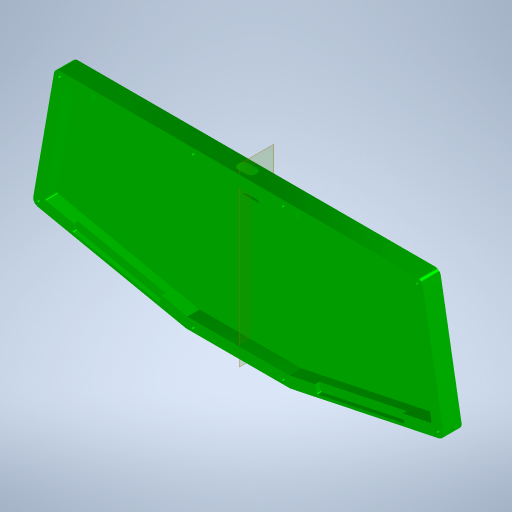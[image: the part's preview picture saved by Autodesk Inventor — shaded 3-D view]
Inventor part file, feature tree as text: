
AUTODESK INVENTOR PART (.ipt)
format: ipt  version: 2023 (Build 270158000, 158)  size: 662,016 bytes
history: native  units: mm
features: reference x28, extrude x7, sketch x7, other x6, fillet x5, plane x2, shell x1, mirror x1, hole x1, projected_geometry x1
ambient origin geometry x8: Origin, YZ Plane, XZ Plane, XY Plane, X Axis, Y Axis, Z Axis, Center Point
bodies: Body1 (feature_tree)
feature tree (59):
  extrude  "Extrusion1"  Depth=1.0mm
  shell  "Shell1"  Thickness=1.0mm
  extrude  "Extrusion7"  Depth=1.0mm
  plane  "Work Plane1"
  extrude  "Extrusion8"  Depth=17.0mm TaperAngle=0.0deg
  extrude  "Extrusion9"  Depth=8.0mm TaperAngle=0.0deg
  plane  "Work Plane2"
  extrude  "Extrusion10"  Depth=18.0mm
  mirror  "Mirror1"
  extrude  "Extrusion12"  Depth=2.0mm
  fillet  "Fillet1"  Radius=2.0mm
  fillet  "Fillet2"  Radius=2.0mm
  fillet  "Fillet3"  Radius=2.0mm
  extrude  "Extrusion13"  Depth=8.0mm TaperAngle=0.0deg
  fillet  "Fillet4"  Radius=98.02976mm
  fillet  "Fillet5"  Radius=10.0mm
  hole  "Hole1"  [1 undecoded]
  sketch  "Sketch1"  dims[d0=1.0mm d1=1.0mm d2=1.0mm]
  reference  "Reference1"
  reference  "Reference2"
  reference  "Reference3"
  reference  "Reference4"
  reference  "Reference5"
  sketch  "Sketch5"  dims[d3=1.0mm d4=1.0mm]
  projected_geometry  "Projected Loop3"
  sketch  "Sketch6"  dims[d5=1.0mm d6=17.0mm d7=0.0mm]
  sketch  "Sketch7"  dims[d8=8.0mm d19=8.0mm d20=0.0mm]
  reference  "Reference12"
  reference  "Reference13"
  reference  "Reference14"
  reference  "Reference15"
  sketch  "Sketch9"  dims[d21=14.486233mm d22=18.0mm]
  sketch  "Sketch12"  dims[d23=0.0mm d24=0.0mm d25=2.0mm d26=2.0mm d27=2.0mm d28=2.0mm]
  reference  "Reference43"
  reference  "Reference44"
  reference  "Reference45"
  reference  "Reference46"
  reference  "Reference47"
  reference  "Reference48"
  reference  "Reference49"
  reference  "Reference50"
  reference  "Reference51"
  reference  "Reference52"
  reference  "Reference53"
  reference  "Reference54"
  reference  "Reference55"
  reference  "Reference57"
  reference  "Reference59"
  reference  "Reference60"
  sketch  "Sketch13"  dims[d29=20.0mm d30=0.0mm d31=30.0mm d32=0.0mm d33=98.02976mm d40=10.0mm d41=0.0mm d42=0.0mm d43=9.0mm d44=3.0mm d45=9.0mm d48=0.5mm d50=0.5mm d51=20.5mm d52=20.5mm d53=20.5mm d56=0.5mm d57=20.5mm d58=20.5mm d60=20.5mm d61=3.0mm d62=0.0mm d63=4.0mm d64=1.0mm d65=4.0mm d66=4.0mm d68=4.0mm d69=2.2mm d70=6.0mm d71=4.0mm d72=8.0mm d73=90.0deg d74=3.0mm d75=0.0mm d78=20.5mm d80=20.5mm]
  reference  "Reference61"
  reference  "Reference63"
  reference  "Reference64"
  other  "<userpath>\Documents\Inventor\atreus-52\Assembly.iam"
  other  "Assembly.iam"
  other  "switch-plates:1"
  other  "atreus52_hotswap:1"
  other  "HRO_TYPE-C-31-M-12:1"
  other  "top-case:1"
note: 1 required parameter value undecoded (feature->parameter linkage not recoverable at this tier; creation-order binding heuristic only, values carry confidence <= 0.55)
